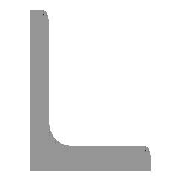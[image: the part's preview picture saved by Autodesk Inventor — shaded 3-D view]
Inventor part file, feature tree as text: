
AUTODESK INVENTOR PART (.ipt)
format: ipt  version: 2024.1 (Build 281209000, 209)  size: 120,832 bytes
history: native  units: mm (DEFAULTED — no unit token found)
features: other x4, sketch x1, plane x1
ambient origin geometry x8: Origin, YZ Plane, XZ Plane, XY Plane, X Axis, Y Axis, Z Axis, Center Point
bodies: Solid1 (feature_tree), Body (feature_tree)
feature tree (6):
  parser-record x1  (decoder bookkeeping rows leaked as tree rows — omitted from the tree; the rows remain in map.json)
  other  "Driven Length"
  other  "Start Plane"
  other  "End Plane"
  sketch  "Sketch3"  dims[d0=25.4mm d1=25.4mm d2=3.175mm d3=3.175mm d4=600.0mm d5=0.0mm d10=0.0mm d11=0.0mm d12=-0.0mm d13=600.0mm d14=3.302mm d15=1.524mm d16=90.0deg d17=600.0mm]
  plane  "Work Plane3"
